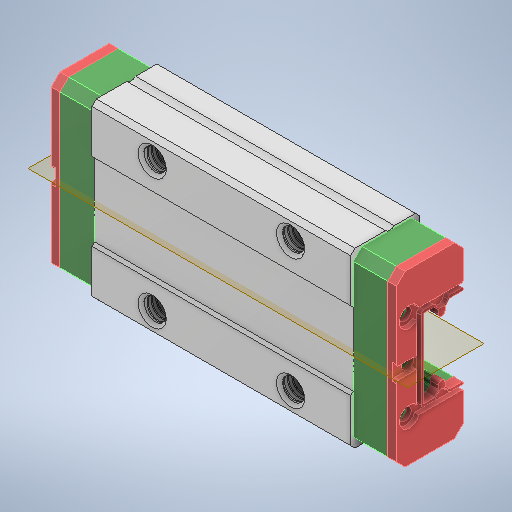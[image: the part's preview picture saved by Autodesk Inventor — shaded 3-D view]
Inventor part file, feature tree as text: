
AUTODESK INVENTOR PART (.ipt)
format: ipt  version: 2025.2 (Build 292293000, 293)  size: 7,666,688 bytes
history: native  units: in
note: dims shown in document units (in); Inventor stores cm internally (conversion verified against a paired STEP export)
features: other x5, plane x1
ambient origin geometry x8: Origin, YZ Plane, XZ Plane, XY Plane, X Axis, Y Axis, Z Axis, Center Point
bodies: Solid1 (feature_tree), Solid2 (feature_tree), Solid3 (feature_tree), Solid4 (feature_tree), Solid5 (feature_tree)
feature tree (6):
  plane  "Work Plane1"
  other  "End Cap 1"
  other  "End Seal 1"
  other  "Block"
  other  "End Cap 2"
  other  "End Seal 2"
